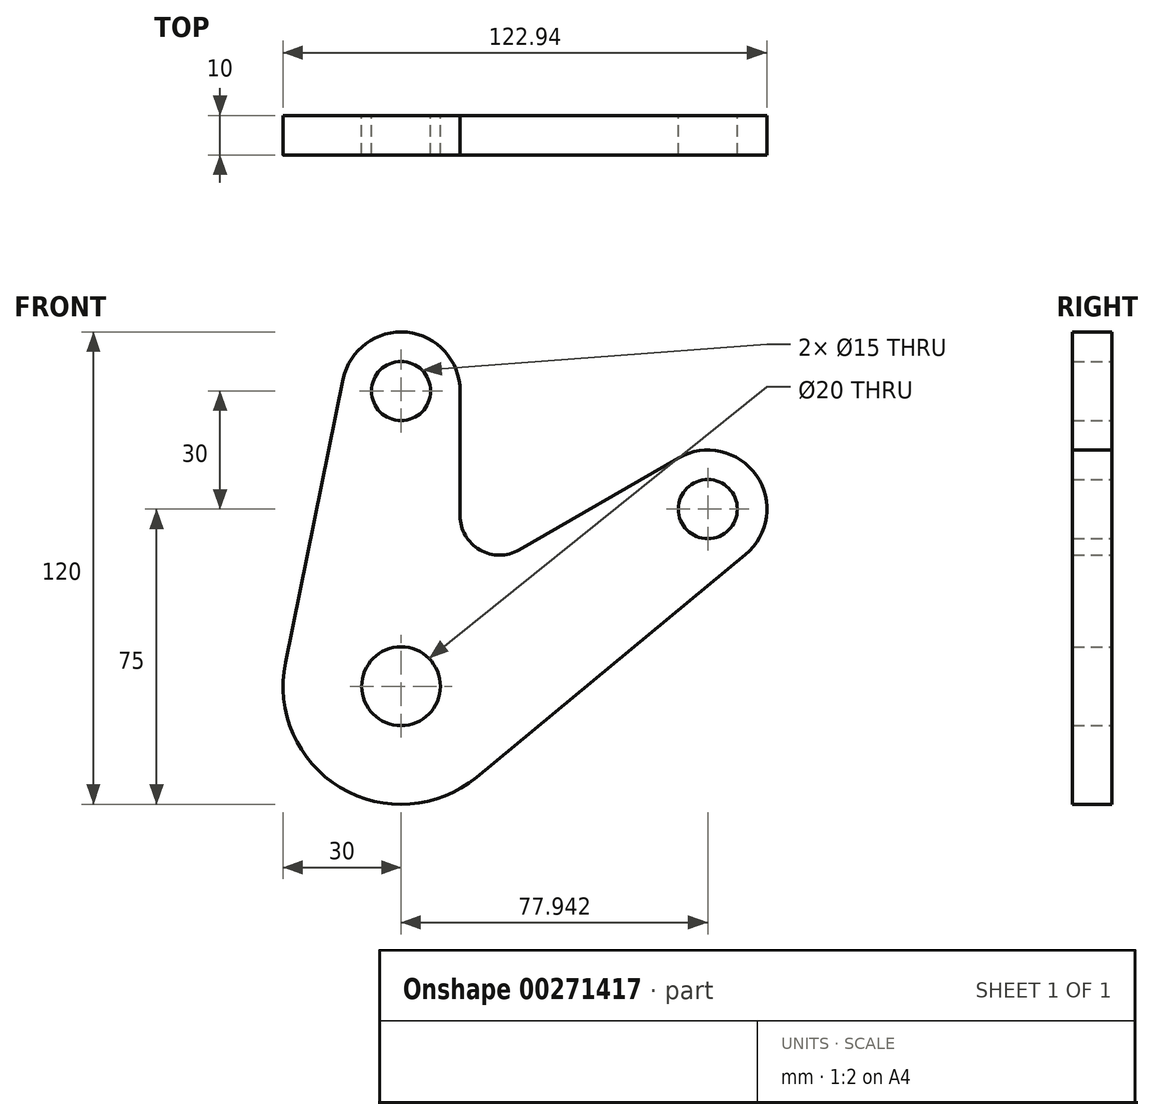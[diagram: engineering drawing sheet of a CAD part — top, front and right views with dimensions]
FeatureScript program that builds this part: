
annotation { "Feature Type Name" : "Feature", "Feature Type Description" : "" }
export const myFeature = defineFeature(function(context is Context, id is Id, definition is map)
    precondition{}
    {
        {
            var Q0;
            Q0=qCreatedBy(makeId("Front.planeOp"),FACE);
            var sketch = newSketch(context, id + "F0", { "sketchPlane" : qUnion([Q0])});
            skCircle(sketch, "E0", {"center": v(0, 0) * mm, "radius": 10 * mm});
            skArc(sketch, "E1", {"start": v(-29.4, 6) * mm, "mid": v(-15.44, -25.72) * mm, "end": v(19.12, -23.12) * mm});
            skLineSegment(sketch, "E2", {"start": v(19.12, -23.12) * mm, "end": v(87.5, 33.44) * mm});
            skLineSegment(sketch, "E3", {"start": v(-29.4, 6) * mm, "end": v(-14.7, 78) * mm});
            skArc(sketch, "E4", {"start": v(15, 75) * mm, "mid": v(1.5, 89.92) * mm, "end": v(-14.7, 78) * mm});
            skLineSegment(sketch, "E5", {"start": v(15, 75) * mm, "end": v(15, 43.3) * mm});
            skArc(sketch, "E6", {"start": v(15, 43.3) * mm, "mid": v(20, 34.64) * mm, "end": v(30, 34.64) * mm});
            skLineSegment(sketch, "E7", {"start": v(30, 34.64) * mm, "end": v(70.44, 58) * mm});
            skArc(sketch, "E8", {"start": v(87.5, 33.44) * mm, "mid": v(90.26, 53.56) * mm, "end": v(70.44, 58) * mm});
            skCircle(sketch, "E9", {"center": v(77.94, 45) * mm, "radius": 7.5 * mm});
            skCircle(sketch, "E10", {"center": v(0, 75) * mm, "radius": 7.5 * mm});
            skLineSegment(sketch, "E11", {"start": v(0, 0) * mm, "end": v(77.94, 45) * mm});
            skLineSegment(sketch, "E12", {"start": v(0, 75) * mm, "end": v(0, 0) * mm});
            skSolve(sketch);
        }
        {
            var Q0;
            Q0 = qSketchRegion(id + "F0", true);
            extrude(context, id + "F1", {"entities" : qUnion([Q0]), "depth" : 10 * mm});
        }
    });
